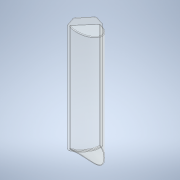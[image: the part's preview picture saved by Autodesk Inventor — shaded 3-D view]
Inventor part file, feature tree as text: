
AUTODESK INVENTOR PART (.ipt)
format: ipt  version: 2022 (Build 260153070, 153G)  size: 4,192,256 bytes
history: native  units: mm
features: sketch x9, extrude x9, plane x7, other x5, thicken_offset x3, fillet x2, projected_geometry x2, surface_op x1
ambient origin geometry x8: Origin, YZ Plane, XZ Plane, XY Plane, X Axis, Y Axis, Z Axis, Center Point
bodies: Body1 (feature_tree), Body2 (feature_tree), Body3 (feature_tree), Body4 (feature_tree)
feature tree (38):
  other  "Work Axis1"
  plane  "Work Plane1"
  sketch  "Sketch3"  dims[d10=1.5875mm d11=0.1mm d13=19.05mm]
  plane  "Work Plane3"
  thicken_offset  "Thicken2"
  thicken_offset  "Thicken6"
  other  "Work Axis3"
  plane  "Work Plane5"
  sketch  "Sketch6"  dims[d24=24.0mm d27=0.0mm d28=0.0mm d29=3.0mm d30=3.0mm]
  extrude  "Extrusion2"  Depth=10.0mm TaperAngle=0.0deg
  extrude  "Extrusion3"  TaperAngle=0.0deg  [1 undecoded]
  extrude  "Extrusion4"  Depth=19.05mm
  extrude  "Extrusion1"  Depth=395.5mm TaperAngle=0.0deg
  plane  "Work Plane9"
  fillet  "Fillet1"  Radius=5.0mm
  extrude  "Extrusion5"  Depth=40.0mm
  thicken_offset  "Thicken7"
  extrude  "Extrusion6"  TaperAngle=0.0deg  [1 undecoded]
  fillet  "Fillet2"  Radius=3.0mm
  extrude  "Extrusion7"  Depth=144.5mm TaperAngle=0.0deg
  plane  "Work Plane11"
  sketch  "Sketch1"  dims[d0=45.72mm d1=0.0mm d2=10.0mm d3=0.0mm]
  other  "Srf1"
  sketch  "Sketch2"  dims[d8=5.0mm d9=0.0mm]
  other  "Srf2"
  sketch  "Sketch4"  dims[d14=75.692mm d15=395.5mm d16=0.0mm d17=5.0mm]
  other  "Srf4"
  sketch  "Sketch5"  dims[d20=58.0mm d23=40.0mm]
  plane  "Work Plane8"
  sketch  "Sketch9"  dims[d31=200.0mm d32=144.5mm d33=0.0mm]
  projected_geometry  "Projected Loop1"
  sketch  "Sketch10"  dims[d34=250.0mm d35=0.0mm d36=3.0mm d37=2.0mm]
  projected_geometry  "Projected Loop2"
  sketch  "Sketch12"  dims[d38=2.0mm d39=0.0mm d40=3.0mm d41=5.0mm d42=2.0mm d43=0.0mm d44=2.0mm d45=40.0mm d46=15.0mm d47=5.0mm d48=2.0mm d49=0.0mm d50=1.75mm]
  plane  "Work Plane10"
  extrude  "ExtrusionSrf1"  Depth=3.0mm
  extrude  "ExtrusionSrf2"  Depth=3.0mm
  surface_op  "Boundary Patch2"
note: 2 required parameter values undecoded (feature->parameter linkage not recoverable at this tier; creation-order binding heuristic only, values carry confidence <= 0.55)
